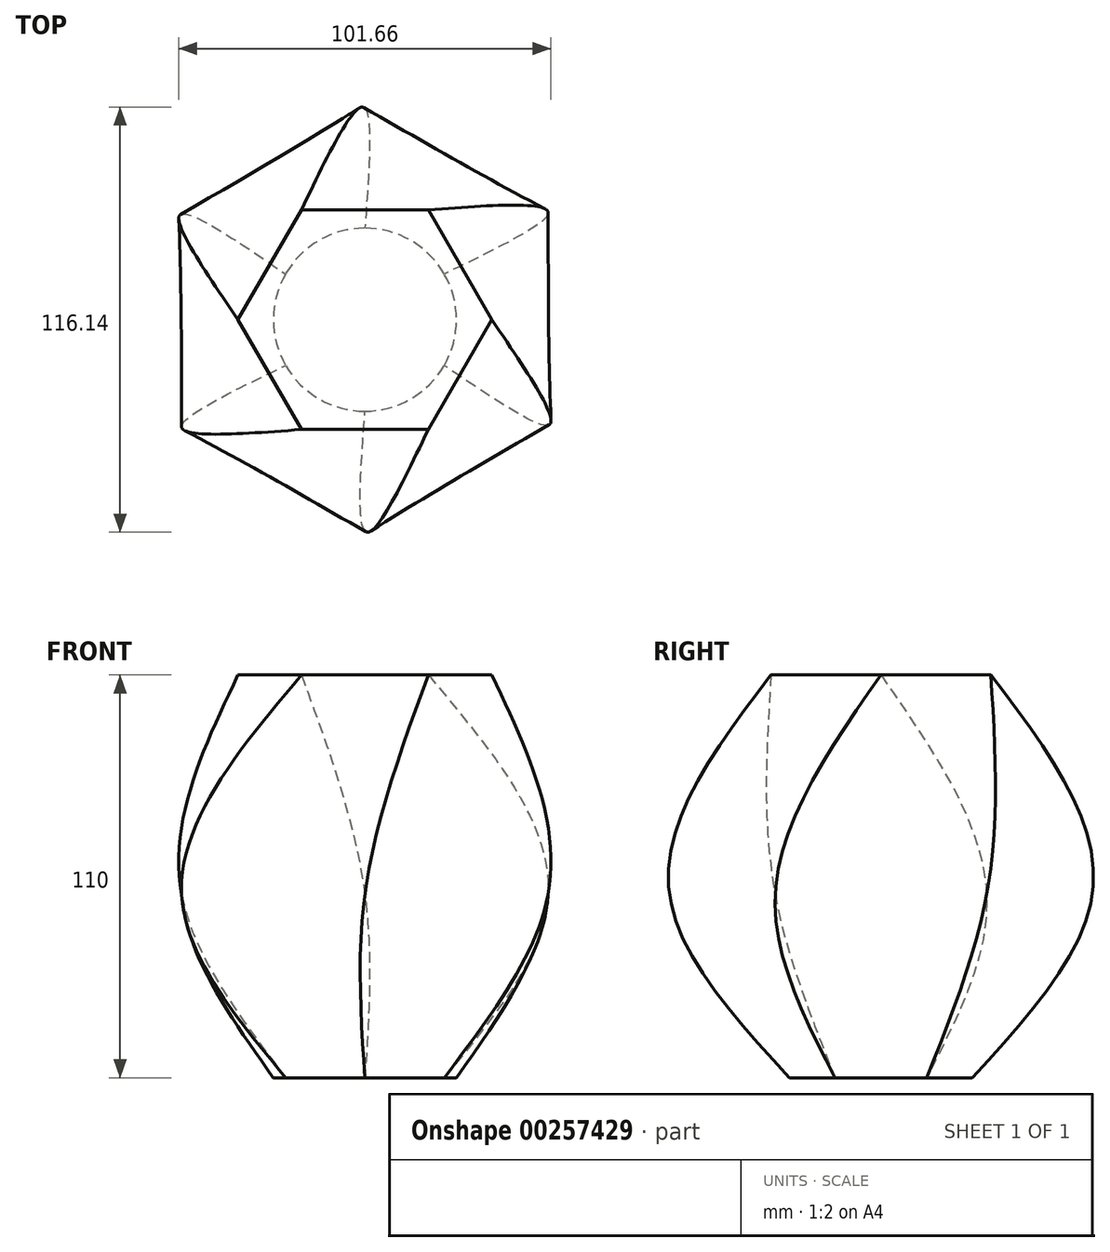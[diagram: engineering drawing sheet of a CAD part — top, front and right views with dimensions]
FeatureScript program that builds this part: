
annotation { "Feature Type Name" : "Feature", "Feature Type Description" : "" }
export const myFeature = defineFeature(function(context is Context, id is Id, definition is map)
    precondition{}
    {
        {
            var Q0;
            Q0=qCreatedBy(makeId("Top.planeOp"),FACE);
            var sketch = newSketch(context, id + "F0", { "sketchPlane" : qUnion([Q0])});
            skCircle(sketch, "E0", {"center": v(0, 0) * mm, "radius": 25 * mm});
            skSolve(sketch);
        }
        {
            var Q0;
            Q0=qCreatedBy(makeId("Top.planeOp"),FACE);
            cPlane(context, id + "F1", {"entities" : qUnion([Q0]), "cplaneType" : CPlaneType.OFFSET, "offset" : 50 * mm, "width" : 150 * mm, "height" : 150 * mm});
        }
        {
            var Q0;
            Q0=qCreatedBy(id+"F1.planeOp",FACE);
            var sketch = newSketch(context, id + "F2", { "sketchPlane" : qUnion([Q0])});
            skCircle(sketch, "E1.cCircle", {"center": v(0, 0) * mm, "radius": 50 * mm, "construction": true});
            skLineSegment(sketch, "E1.0", {"start": v(50, 28.87) * mm, "end": v(50, -28.87) * mm});
            skLineSegment(sketch, "E1.1", {"start": v(50, -28.87) * mm, "end": v(0, -57.74) * mm});
            skLineSegment(sketch, "E1.2", {"start": v(0, -57.74) * mm, "end": v(-50, -28.87) * mm});
            skLineSegment(sketch, "E1.3", {"start": v(-50, -28.87) * mm, "end": v(-50, 28.87) * mm});
            skLineSegment(sketch, "E1.4", {"start": v(-50, 28.87) * mm, "end": v(0, 57.74) * mm});
            skLineSegment(sketch, "E1.5", {"start": v(0, 57.74) * mm, "end": v(50, 28.87) * mm});
            skPoint(sketch, "E1.0.midPoint", {"position": v(50, 0) * mm});
            skSolve(sketch);
        }
        {
            var Q0;
            Q0=qCreatedBy(id+"F1.planeOp",FACE);
            cPlane(context, id + "F3", {"entities" : qUnion([Q0]), "cplaneType" : CPlaneType.OFFSET, "offset" : 60 * mm, "width" : 150 * mm, "height" : 150 * mm});
        }
        {
            var Q0;
            Q0=qCreatedBy(id+"F3.planeOp",FACE);
            var sketch = newSketch(context, id + "F4", { "sketchPlane" : qUnion([Q0])});
            skCircle(sketch, "E2.cCircle", {"center": v(0, 0) * mm, "radius": 30 * mm, "construction": true});
            skLineSegment(sketch, "E2.0", {"start": v(-17.32, 30) * mm, "end": v(17.32, 30) * mm});
            skLineSegment(sketch, "E2.1", {"start": v(17.32, 30) * mm, "end": v(34.64, 0) * mm});
            skLineSegment(sketch, "E2.2", {"start": v(34.64, 0) * mm, "end": v(17.32, -30) * mm});
            skLineSegment(sketch, "E2.3", {"start": v(17.32, -30) * mm, "end": v(-17.32, -30) * mm});
            skLineSegment(sketch, "E2.4", {"start": v(-17.32, -30) * mm, "end": v(-34.64, 0) * mm});
            skLineSegment(sketch, "E2.5", {"start": v(-34.64, 0) * mm, "end": v(-17.32, 30) * mm});
            skPoint(sketch, "E2.0.midPoint", {"position": v(0, 30) * mm});
            skSolve(sketch);
        }
        {
            var Q0;
            Q0=makeQuery(id+"F4.imprint","IMPRINT",FACE,{"disambiguationData":[TD([[makeQuery(id+"F4.imprint","IMPRINT",EDGE,{"derivedFrom":sQuery(id+"F4.wireOp",EDGE,"E2.0")}),-1.0]])]});
            var Q1;
            Q1=makeQuery(id+"F2.imprint","IMPRINT",FACE,{"disambiguationData":[TD([[makeQuery(id+"F2.imprint","IMPRINT",EDGE,{"derivedFrom":sQuery(id+"F2.wireOp",EDGE,"E1.0")}),-1.0]])]});
            var Q2;
            Q2=makeQuery(id+"F0.imprint","IMPRINT",FACE,{"disambiguationData":[TD([[makeQuery(id+"F0.imprint","IMPRINT",EDGE,{"derivedFrom":sQuery(id+"F0.wireOp",EDGE,"E0")}),1.0]])]});
            loft(context, id + "F5", {"sheetProfilesArray" : [{ "sheetProfileEntities" : qUnion([Q0]) }, { "sheetProfileEntities" : qUnion([Q1]) }, { "sheetProfileEntities" : qUnion([Q2]) }]});
        }
    });
